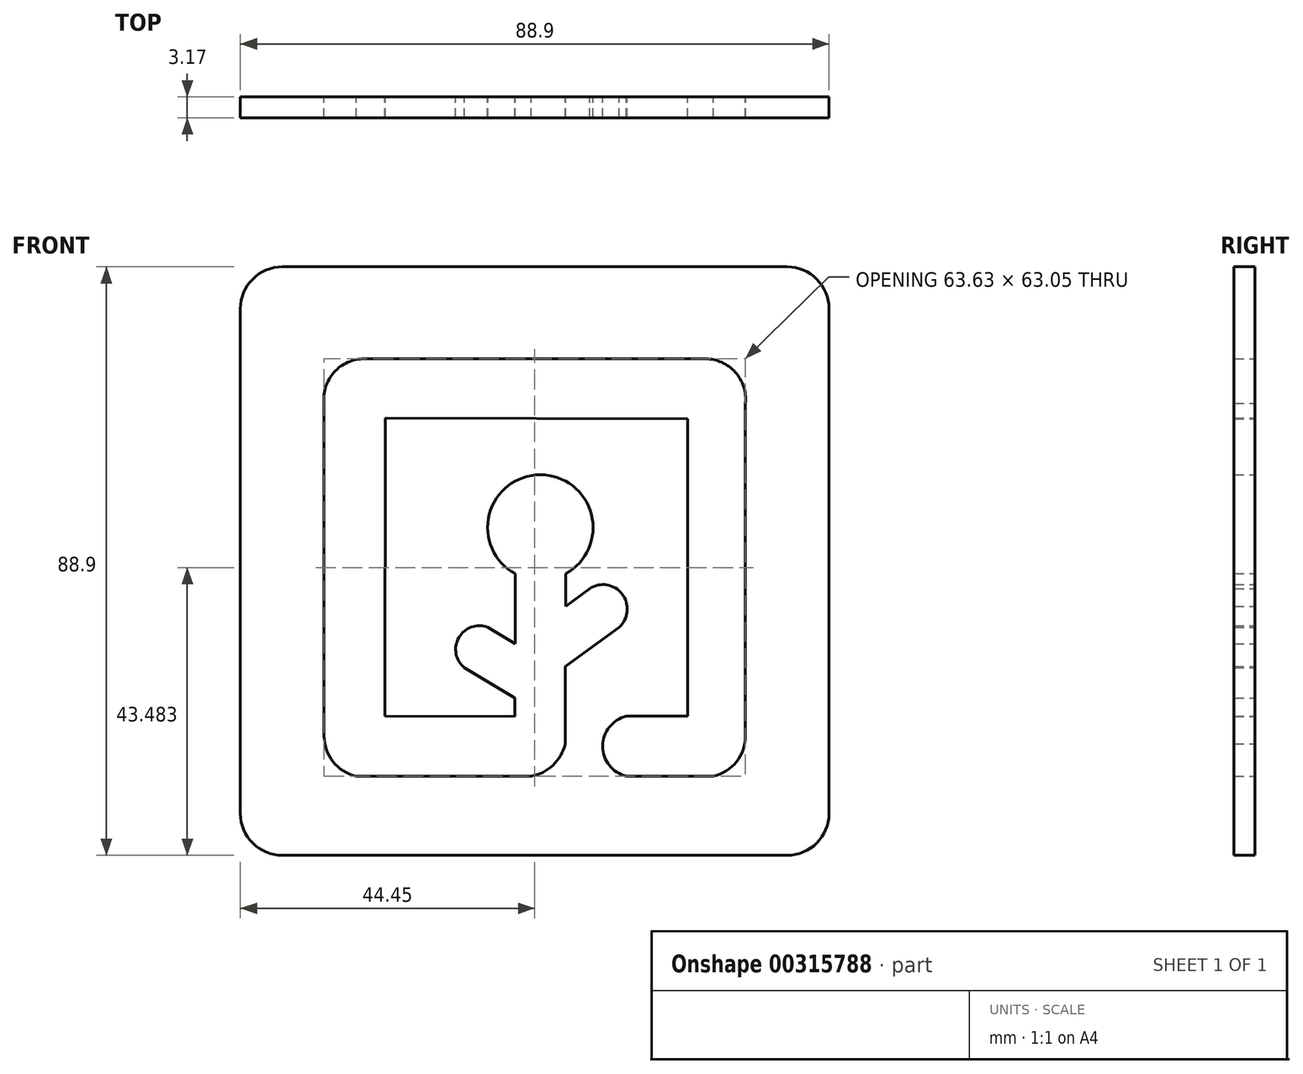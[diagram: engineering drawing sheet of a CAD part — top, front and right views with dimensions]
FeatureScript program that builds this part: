
annotation { "Feature Type Name" : "Feature", "Feature Type Description" : "" }
export const myFeature = defineFeature(function(context is Context, id is Id, definition is map)
    precondition{}
    {
        {
            var Q0;
            Q0=qCreatedBy(makeId("Front.planeOp"),FACE);
            var sketch = newSketch(context, id + "F0", { "sketchPlane" : qUnion([Q0])});
            skLineSegment(sketch, "E0", {"start": v(23.12, 15.16) * mm, "end": v(23.12, -29.78) * mm});
            skLineSegment(sketch, "E1", {"start": v(31.81, -32.76) * mm, "end": v(31.81, 17.48) * mm});
            skLineSegment(sketch, "E2", {"start": v(0, 43.38) * mm, "end": v(0, -69.91) * mm, "construction": true});
            skLineSegment(sketch, "E3", {"start": v(-73.66, 0) * mm, "end": v(31.81, 0) * mm, "construction": true});
            skPoint(sketch, "E4.visualSharp", {"position": v(-31.23, 23.83) * mm});
            skArc(sketch, "E5", {"start": v(26.96, -38.84) * mm, "mid": v(30.45, -36.65) * mm, "end": v(31.81, -32.76) * mm});
            skLineSegment(sketch, "E6", {"start": v(26.96, -38.84) * mm, "end": v(13.81, -38.84) * mm});
            skArc(sketch, "E7", {"start": v(13.81, -29.78) * mm, "mid": v(10.27, -34.31) * mm, "end": v(13.81, -38.84) * mm});
            skLineSegment(sketch, "E8", {"start": v(13.81, -29.78) * mm, "end": v(23.12, -29.78) * mm});
            skLineSegment(sketch, "E9", {"start": v(-22.54, 15.27) * mm, "end": v(23.12, 15.16) * mm});
            skLineSegment(sketch, "E10", {"start": v(-22.54, 15.27) * mm, "end": v(-22.65, -29.75) * mm});
            skLineSegment(sketch, "E11", {"start": v(-22.65, -29.75) * mm, "end": v(-3.02, -29.8) * mm});
            skLineSegment(sketch, "E12", {"start": v(-3.02, -29.8) * mm, "end": v(-3.02, -27.05) * mm});
            skLineSegment(sketch, "E13", {"start": v(-3.02, -27.05) * mm, "end": v(-10.6, -22.48) * mm});
            skArc(sketch, "E14", {"start": v(-7.07, -16.36) * mm, "mid": v(-11.46, -17.9) * mm, "end": v(-10.6, -22.48) * mm});
            skLineSegment(sketch, "E15", {"start": v(-7.07, -16.36) * mm, "end": v(-2.96, -18.8) * mm});
            skLineSegment(sketch, "E16", {"start": v(-2.96, -18.8) * mm, "end": v(-2.96, -8.26) * mm});
            skLineSegment(sketch, "E17", {"start": v(-2.96, -8.26) * mm, "end": v(4.66, -8.26) * mm, "construction": true});
            skLineSegment(sketch, "E18", {"start": v(4.66, -8.26) * mm, "end": v(4.66, -13.17) * mm});
            skLineSegment(sketch, "E19", {"start": v(4.66, -13.17) * mm, "end": v(8.27, -10.5) * mm});
            skArc(sketch, "E20", {"start": v(4.66, -8.26) * mm, "mid": v(0.85, 6.7) * mm, "end": v(-2.96, -8.26) * mm});
            skArc(sketch, "E21", {"start": v(12.75, -16.33) * mm, "mid": v(13.22, -11.34) * mm, "end": v(8.27, -10.5) * mm});
            skLineSegment(sketch, "E22", {"start": v(12.75, -16.33) * mm, "end": v(4.6, -22.29) * mm});
            skLineSegment(sketch, "E23", {"start": v(4.6, -22.29) * mm, "end": v(4.6, -33.96) * mm});
            skArc(sketch, "E24", {"start": v(-0.56, -38.84) * mm, "mid": v(2.75, -37.17) * mm, "end": v(4.6, -33.96) * mm});
            skLineSegment(sketch, "E25", {"start": v(-0.56, -38.84) * mm, "end": v(-26.96, -38.84) * mm});
            skLineSegment(sketch, "E26", {"start": v(0, 24.2) * mm, "end": v(25.76, 24.2) * mm});
            skArc(sketch, "E27", {"start": v(31.81, 17.48) * mm, "mid": v(30.28, 22.2) * mm, "end": v(25.76, 24.2) * mm});
            skLineSegment(sketch, "E28.MirrorCS", {"start": v(0, 24.2) * mm, "end": v(-25.76, 24.2) * mm});
            skArc(sketch, "E29.MirrorCS", {"start": v(-31.81, 17.48) * mm, "mid": v(-30.28, 22.2) * mm, "end": v(-25.76, 24.2) * mm});
            skLineSegment(sketch, "E30.MirrorCS", {"start": v(-31.81, -32.76) * mm, "end": v(-31.81, 17.48) * mm});
            skArc(sketch, "E31.MirrorCS", {"start": v(-26.96, -38.84) * mm, "mid": v(-30.45, -36.65) * mm, "end": v(-31.81, -32.76) * mm});
            skSolve(sketch);
        }
        {
            var Q0;
            Q0=qCreatedBy(makeId("Front.planeOp"),FACE);
            var sketch = newSketch(context, id + "F1", { "sketchPlane" : qUnion([Q0])});
            skLineSegment(sketch, "E32.bottom", {"start": v(-38.1, 38.1) * mm, "end": v(38.1, 38.1) * mm});
            skLineSegment(sketch, "E32.top", {"start": v(-38.1, -50.8) * mm, "end": v(38.1, -50.8) * mm});
            skLineSegment(sketch, "E32.left", {"start": v(-44.45, 31.75) * mm, "end": v(-44.45, -44.45) * mm});
            skLineSegment(sketch, "E32.right", {"start": v(44.45, 31.75) * mm, "end": v(44.45, -44.45) * mm});
            skPoint(sketch, "E33.visualSharp", {"position": v(-44.45, 38.1) * mm});
            skArc(sketch, "E33.filletArc", {"start": v(-38.1, 38.1) * mm, "mid": v(-42.6, 36.24) * mm, "end": v(-44.45, 31.75) * mm});
            skPoint(sketch, "E34.visualSharp", {"position": v(-44.45, -50.8) * mm});
            skArc(sketch, "E34.filletArc", {"start": v(-44.45, -44.45) * mm, "mid": v(-42.6, -48.94) * mm, "end": v(-38.1, -50.8) * mm});
            skPoint(sketch, "E35.visualSharp", {"position": v(44.45, -50.8) * mm});
            skArc(sketch, "E35.filletArc", {"start": v(38.1, -50.8) * mm, "mid": v(42.6, -48.94) * mm, "end": v(44.45, -44.45) * mm});
            skPoint(sketch, "E36.visualSharp", {"position": v(44.45, 38.1) * mm});
            skArc(sketch, "E36.filletArc", {"start": v(44.45, 31.75) * mm, "mid": v(42.6, 36.24) * mm, "end": v(38.1, 38.1) * mm});
            skSolve(sketch);
        }
        {
            var Q0;
            Q0=qSketchRegion(id+"F1",true);
            extrude(context, id + "F2", {"entities" : qUnion([Q0]), "depth" : 3.17 * mm});
        }
        {
            var Q0;
            Q0=qSketchRegion(id+"F0",true);
            extrude(context, id + "F3", {"entities" : qUnion([Q0]), "operationType" : NewBodyOperationType.REMOVE, "endBound" : BoundingType.THROUGH_ALL, "depth" : 6.35 * mm});
        }
    });
